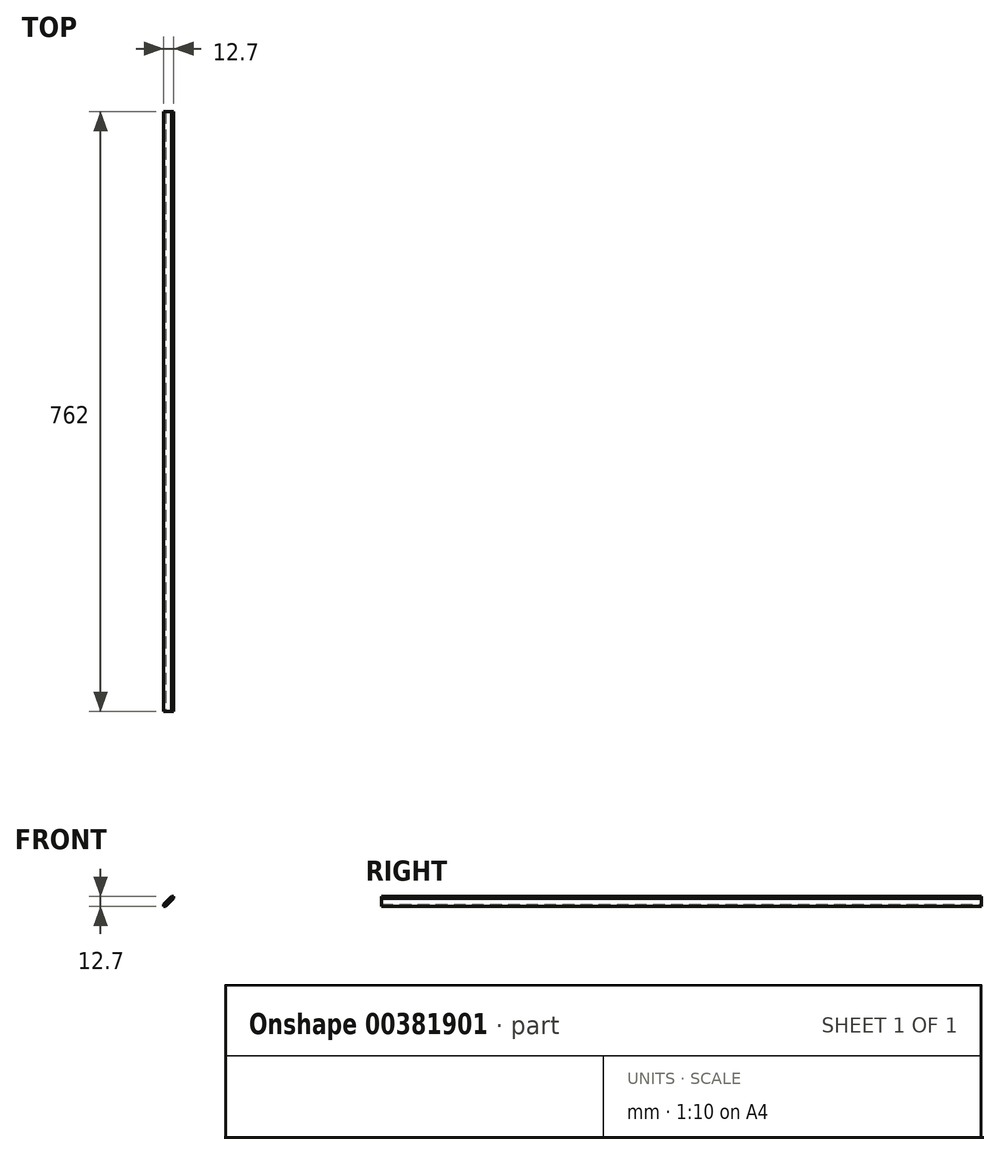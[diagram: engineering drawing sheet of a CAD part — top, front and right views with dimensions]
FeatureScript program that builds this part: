
annotation { "Feature Type Name" : "Feature", "Feature Type Description" : "" }
export const myFeature = defineFeature(function(context is Context, id is Id, definition is map)
    precondition{}
    {
        {
            var Q0;
            Q0=qCreatedBy(makeId("Top.planeOp"),FACE);
            var sketch = newSketch(context, id + "F0", { "sketchPlane" : qUnion([Q0])});
            skLineSegment(sketch, "E0.bottom", {"start": v(-59.88, 701.32) * mm, "end": v(-47.18, 701.32) * mm});
            skLineSegment(sketch, "E0.top", {"start": v(-59.88, -60.68) * mm, "end": v(-47.18, -60.68) * mm});
            skLineSegment(sketch, "E0.left", {"start": v(-59.88, 701.32) * mm, "end": v(-59.88, -60.68) * mm});
            skLineSegment(sketch, "E0.right", {"start": v(-47.18, 701.32) * mm, "end": v(-47.18, -60.68) * mm});
            skSolve(sketch);
        }
        {
            var Q0;
            Q0 = qSketchRegion(id + "F0", true);
            extrude(context, id + "F1", {"entities" : qUnion([Q0]), "depth" : 12.7 * mm});
        }
        {
            var Q0;
            Q0=makeQuery(id+"F1.opExtrude","CAP_EDGE",EDGE,{"disambiguationData":[OSD([sQuery(id+"F0.wireOp",EDGE,"E0.left")])],"isStart":false});
            var Q1;
            Q1=makeQuery(id+"F1.opExtrude","CAP_EDGE",EDGE,{"disambiguationData":[OSD([sQuery(id+"F0.wireOp",EDGE,"E0.right")])],"isStart":true});
            chamfer(context, id + "F2", {"entities" : qUnion([Q0, Q1]), "width" : 10.16 * mm, "tangentPropagation" : true});
        }
    });
